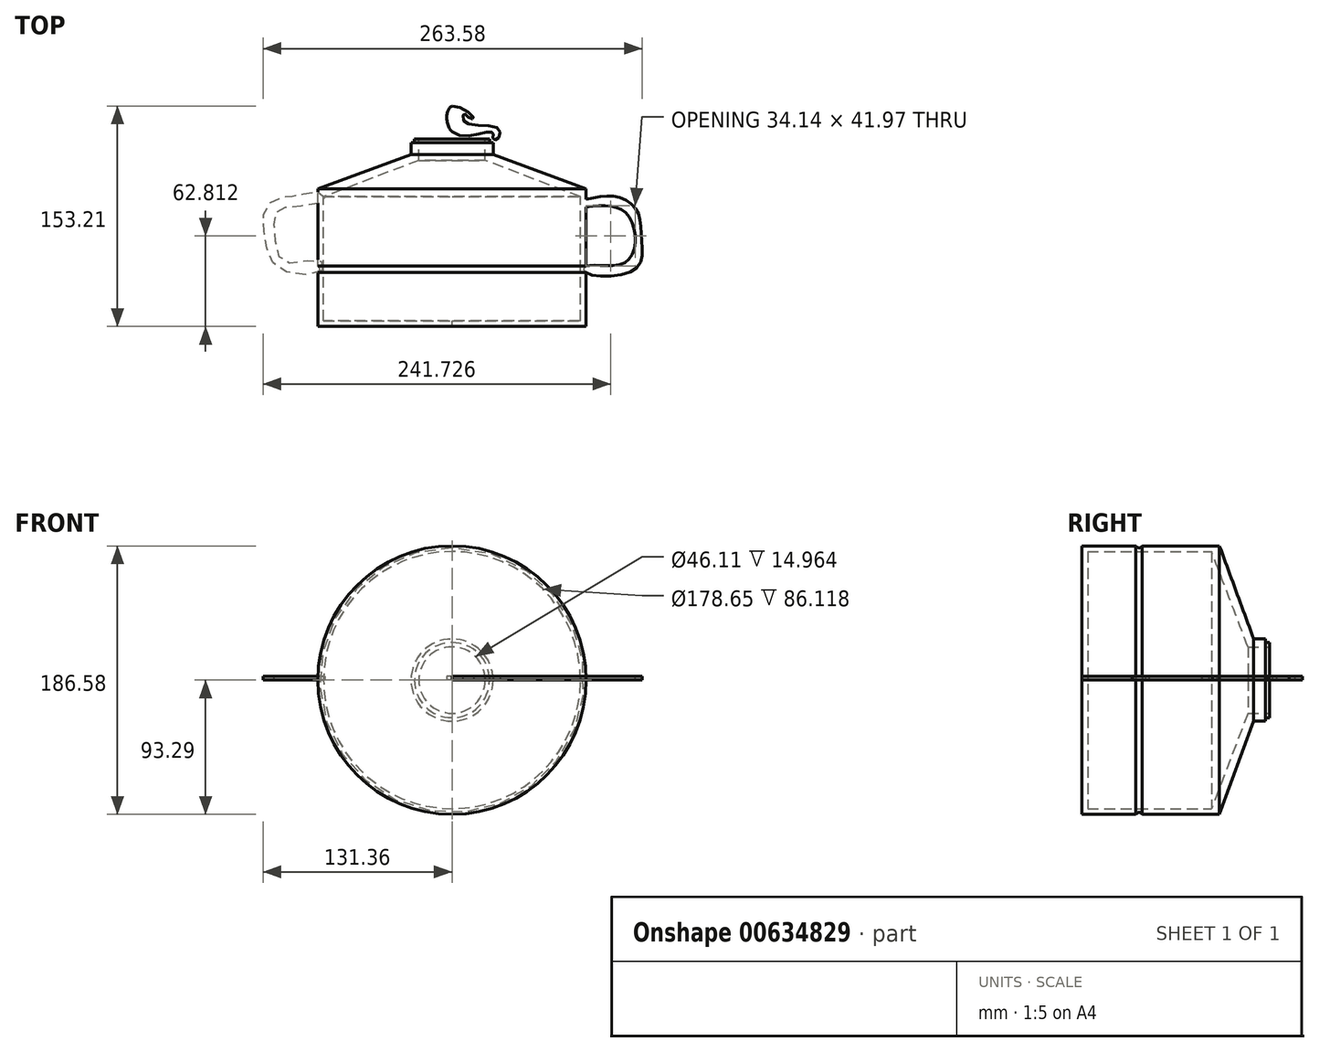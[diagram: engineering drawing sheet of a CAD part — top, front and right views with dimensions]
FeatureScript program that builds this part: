
annotation { "Feature Type Name" : "Feature", "Feature Type Description" : "" }
export const myFeature = defineFeature(function(context is Context, id is Id, definition is map)
    precondition{}
    {
        {
            var Q0;
            Q0=qCreatedBy(makeId("Top.planeOp"),FACE);
            var sketch = newSketch(context, id + "F0", { "sketchPlane" : qUnion([Q0])});
            skLineSegment(sketch, "E0", {"start": v(0, 54.82) * mm, "end": v(0, -73.44) * mm});
            skLineSegment(sketch, "E1", {"start": v(0, -73.44) * mm, "end": v(89.32, -73.44) * mm});
            skLineSegment(sketch, "E2", {"start": v(89.32, -73.44) * mm, "end": v(89.32, -31.6) * mm});
            skLineSegment(sketch, "E3", {"start": v(89.32, -31.6) * mm, "end": v(89.32, 12.67) * mm});
            skLineSegment(sketch, "E4", {"start": v(89.32, 12.67) * mm, "end": v(23.06, 38.02) * mm});
            skLineSegment(sketch, "E5", {"start": v(23.06, 38.02) * mm, "end": v(23.06, 52.98) * mm});
            skLineSegment(sketch, "E6", {"start": v(23.06, 52.98) * mm, "end": v(26.11, 52.98) * mm});
            skLineSegment(sketch, "E7", {"start": v(26.11, 52.98) * mm, "end": v(26.11, 50.24) * mm});
            skLineSegment(sketch, "E8", {"start": v(26.11, 50.24) * mm, "end": v(28.55, 50.24) * mm});
            skLineSegment(sketch, "E9", {"start": v(28.55, 50.24) * mm, "end": v(28.55, 41.99) * mm});
            skLineSegment(sketch, "E10", {"start": v(28.55, 41.99) * mm, "end": v(93.3, 18.17) * mm});
            skLineSegment(sketch, "E11", {"start": v(93.3, 18.17) * mm, "end": v(93.3, -77.41) * mm});
            skLineSegment(sketch, "E12", {"start": v(93.3, -77.41) * mm, "end": v(0, -77.41) * mm});
            skLineSegment(sketch, "E13", {"start": v(0, -77.41) * mm, "end": v(0, 75.58) * mm});
            skLineSegment(sketch, "E14", {"start": v(0, 75.58) * mm, "end": v(0, -77.41) * mm});
            skFitSpline(sketch, "E15", {"points": [v(23.06, 57.26) * mm, v(28.55, 56.95) * mm, v(28.55, 52.98) * mm, v(31.6, 52.98) * mm, v(31.91, 60.31) * mm, v(8.7, 64.59) * mm, v(8.4, 70.4) * mm, v(11.76, 67.64) * mm, v(15.12, 67.34) * mm, v(0, 75.58) * mm, v(0, 57.87) * mm, v(23.06, 57.26) * mm]});
            skFitSpline(sketch, "E16", {"points": [v(93.3, 10.9) * mm, v(114.46, 12.75) * mm, v(128.72, 2.84) * mm, v(131.81, -17.61) * mm, v(127.17, -37.75) * mm, v(93.3, -39.92) * mm, v(93.3, -35.58) * mm, v(121.59, -32.17) * mm, v(122.2, 0) * mm, v(93.3, 5.63) * mm], "startDerivative": vector(199.46, 44) * mm, "endDerivative": vector(-264.17, -25.52) * mm});
            skFitSpline(sketch, "E17", {"points": [v(-90.31, -38.48) * mm, v(-119.53, -37.63) * mm, v(-129.7, -17.64) * mm, v(-129.06, 5.65) * mm, v(-115.24, 12.96) * mm, v(-107.82, 13.55) * mm, v(-91.5, 15.67) * mm, v(-88.72, 10.55) * mm, v(-108.83, 5.96) * mm, v(-122.1, 2.07) * mm, v(-123.31, -15) * mm, v(-115.99, -32.8) * mm, v(-92.03, -31.44) * mm, v(-90.31, -38.48) * mm]});
            skSolve(sketch);
        }
        {
            var Q0;
            {var subQ0=sQuery(id+"F0.wireOp",EDGE,"E15");var subQ1=sQuery(id+"F0.wireOp",EDGE,"E14");var subQ2=makeQuery(id+"F0.imprint","INTERSECT",VERTEX,{"disambiguationData":[OD(0.0)],"derivedFrom":[subQ1,subQ0]});Q0=makeQuery(id+"F0.imprint","IMPRINT",FACE,{"disambiguationData":[TD([[makeQuery(id+"F0.imprint","IMPRINT",EDGE,{"disambiguationData":[TD([[subQ2,-1.0]])],"derivedFrom":subQ1}),1.0]])]});}
            var Q1;
            {var subQ0=sQuery(id+"F0.wireOp",EDGE,"E1");Q1=makeQuery(id+"F0.imprint","IMPRINT",FACE,{"disambiguationData":[TD([[makeQuery(id+"F0.imprint","IMPRINT",EDGE,{"derivedFrom":subQ0}),-1.0]])]});}
            var Q2;
            Q2=sQuery(id+"F0.wireOp",EDGE,"E14");
            revolve(context, id + "F1", {"entities" : qUnion([Q0, Q1]), "axis" : qUnion([Q2]), "revolveType" : RevolveType.FULL});
        }
        {
            var Q0;
            Q0 = qSketchRegion(id + "F0", true);
            extrude(context, id + "F2", {"entities" : qUnion([Q0]), "depth" : 2.8 * mm, "offsetDistance" : 25.4 * mm});
        }
    });
